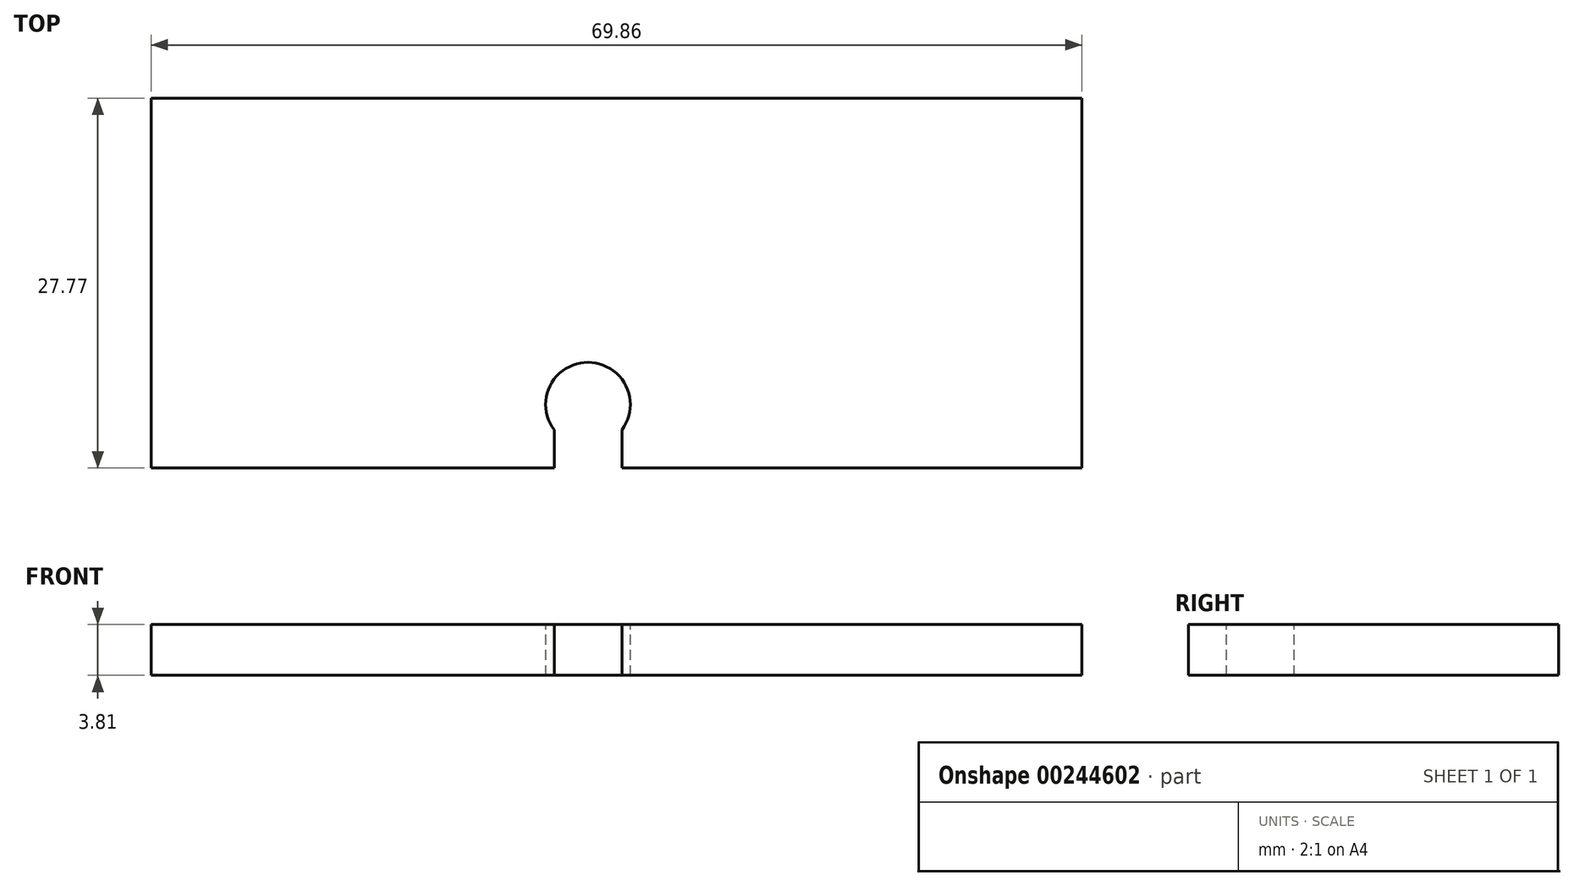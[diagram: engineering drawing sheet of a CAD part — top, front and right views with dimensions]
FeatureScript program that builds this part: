
annotation { "Feature Type Name" : "Feature", "Feature Type Description" : "" }
export const myFeature = defineFeature(function(context is Context, id is Id, definition is map)
    precondition{}
    {
        {
            var Q0;
            Q0=qCreatedBy(makeId("Top.planeOp"),FACE);
            var sketch = newSketch(context, id + "F0", { "sketchPlane" : qUnion([Q0])});
            skLineSegment(sketch, "E0.bottom", {"start": v(-32.8, 12.07) * mm, "end": v(37.07, 12.07) * mm});
            skLineSegment(sketch, "E0.top", {"start": v(-32.8, -15.7) * mm, "end": v(37.07, -15.7) * mm});
            skLineSegment(sketch, "E0.left", {"start": v(-32.8, 12.07) * mm, "end": v(-32.8, -15.7) * mm});
            skLineSegment(sketch, "E0.right", {"start": v(37.07, 12.07) * mm, "end": v(37.07, -15.7) * mm});
            skSolve(sketch);
        }
        {
            var Q0;
            Q0 = qSketchRegion(id + "F0", true);
            extrude(context, id + "F1", {"entities" : qUnion([Q0]), "depth" : 3.8 * mm});
        }
        {
            var Q0;
            Q0=makeQuery(id+"F1.opExtrude","CAP_FACE",FACE,{"disambiguationData":[OSD([sQuery(id+"F0.wireOp",EDGE,"E0.bottom"),sQuery(id+"F0.wireOp",EDGE,"E0.top"),sQuery(id+"F0.wireOp",EDGE,"E0.left"),sQuery(id+"F0.wireOp",EDGE,"E0.right")])],"isStart":false});
            var sketch = newSketch(context, id + "F2", { "sketchPlane" : qUnion([Q0])});
            skArc(sketch, "E1", {"start": v(2.54, -12.85) * mm, "mid": v(0, -7.77) * mm, "end": v(-2.54, -12.85) * mm});
            skLineSegment(sketch, "E2", {"start": v(2.54, -12.85) * mm, "end": v(2.54, -15.7) * mm});
            skLineSegment(sketch, "E3", {"start": v(-2.54, -12.85) * mm, "end": v(-2.54, -15.7) * mm});
            skLineSegment(sketch, "E4", {"start": v(-2.54, -15.7) * mm, "end": v(2.54, -15.7) * mm});
            skSolve(sketch);
        }
        {
            var Q0;
            Q0 = qSketchRegion(id + "F2", true);
            extrude(context, id + "F3", {"entities" : qUnion([Q0]), "operationType" : NewBodyOperationType.REMOVE, "oppositeDirection" : true, "depth" : 25.4 * mm});
        }
    });
